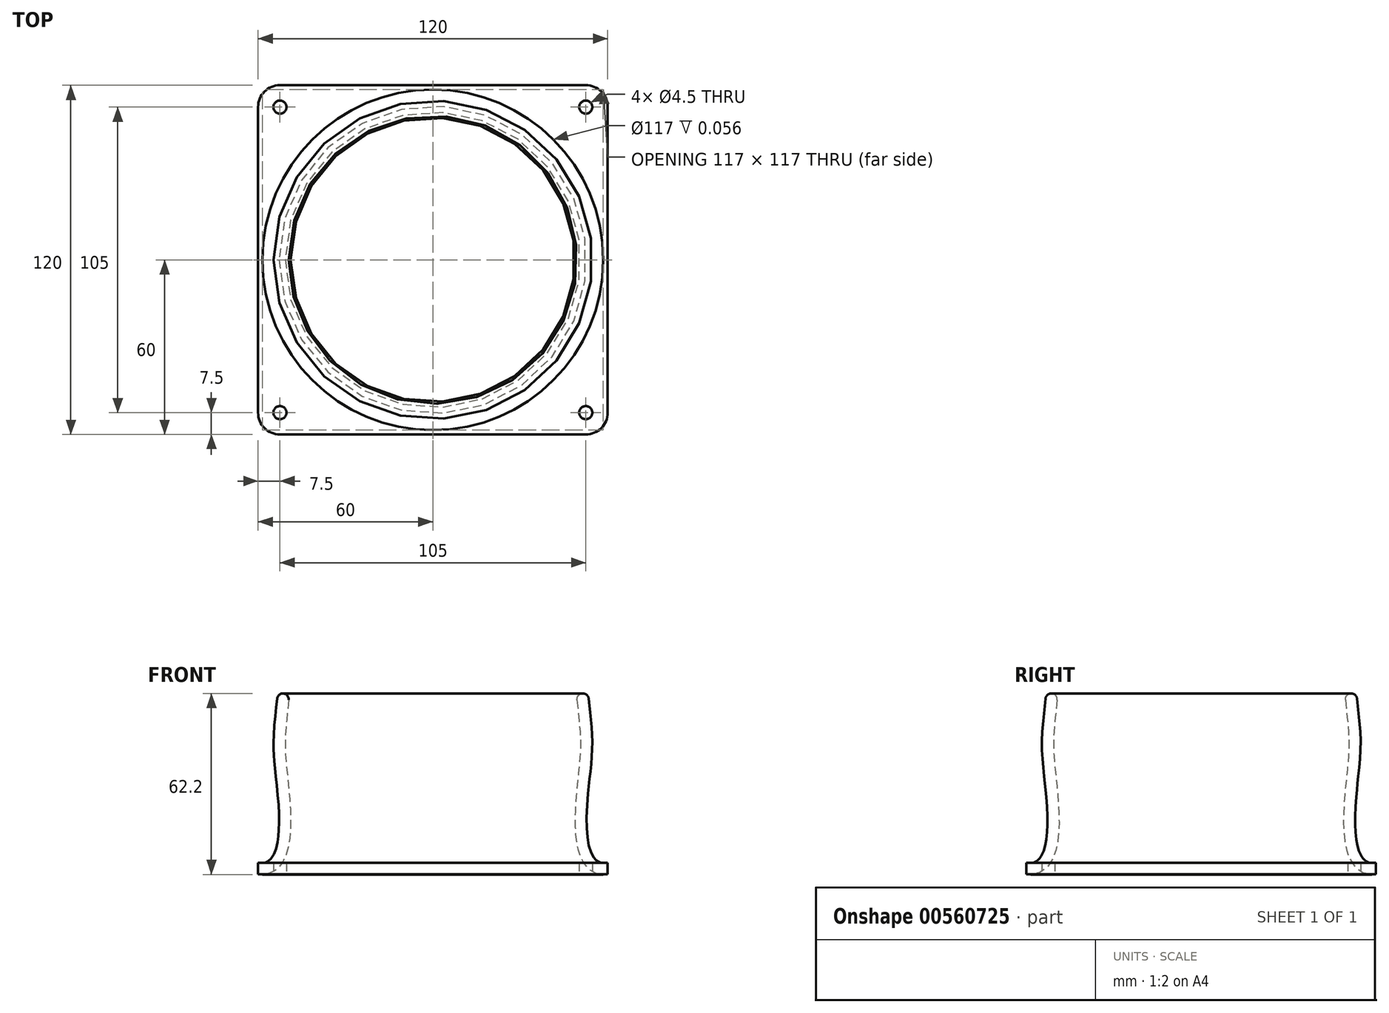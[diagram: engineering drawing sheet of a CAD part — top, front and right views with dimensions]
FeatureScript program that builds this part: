
annotation { "Feature Type Name" : "Feature", "Feature Type Description" : "" }
export const myFeature = defineFeature(function(context is Context, id is Id, definition is map)
    precondition{}
    {
        {
            var Q0;
            Q0=qCreatedBy(makeId("Top.planeOp"),FACE);
            var sketch = newSketch(context, id + "F0", { "sketchPlane" : qUnion([Q0])});
            skLineSegment(sketch, "E0.0", {"start": v(-52.5, 60) * mm, "end": v(52.5, 60) * mm});
            skLineSegment(sketch, "E0.1", {"start": v(-60, -52.5) * mm, "end": v(-60, 52.5) * mm});
            skLineSegment(sketch, "E0.2", {"start": v(-52.5, -60) * mm, "end": v(52.5, -60) * mm});
            skLineSegment(sketch, "E0.3", {"start": v(60, -52.5) * mm, "end": v(60, 52.5) * mm});
            skArc(sketch, "E1", {"start": v(52.5, 60) * mm, "mid": v(57.8, 57.8) * mm, "end": v(60, 52.5) * mm});
            skArc(sketch, "E2.1.1", {"start": v(-60, 52.5) * mm, "mid": v(-57.8, 57.8) * mm, "end": v(-52.5, 60) * mm});
            skArc(sketch, "E2.2.1", {"start": v(-52.5, -60) * mm, "mid": v(-57.8, -57.8) * mm, "end": v(-60, -52.5) * mm});
            skArc(sketch, "E2.3.1", {"start": v(60, -52.5) * mm, "mid": v(57.8, -57.8) * mm, "end": v(52.5, -60) * mm});
            skPoint(sketch, "E2.center", {"position": v(0, 0) * mm});
            skCircle(sketch, "E3", {"center": v(0, 0) * mm, "radius": 58.5 * mm});
            skCircle(sketch, "E4", {"center": v(-52.5, 52.5) * mm, "radius": 2.25 * mm});
            skCircle(sketch, "E5", {"center": v(52.5, 52.5) * mm, "radius": 2.25 * mm});
            skCircle(sketch, "E6", {"center": v(52.5, -52.5) * mm, "radius": 2.25 * mm});
            skCircle(sketch, "E7", {"center": v(-52.5, -52.5) * mm, "radius": 2.25 * mm});
            skSolve(sketch);
        }
        {
            var Q0;
            Q0 = qSketchRegion(id + "F0", true);
            extrude(context, id + "F1", {"entities" : qUnion([Q0]), "depth" : 4 * mm, "offsetDistance" : 25 * mm});
        }
        {
            var Q0;
            Q0=qCreatedBy(makeId("Front.planeOp"),FACE);
            var sketch = newSketch(context, id + "F2", { "sketchPlane" : qUnion([Q0])});
            skPoint(sketch, "E8.0", {"position": v(0, 0) * mm});
            skLineSegment(sketch, "E9", {"start": v(0, 0) * mm, "end": v(0, 73.15) * mm});
            skSolve(sketch);
        }
        {
            var Q0;
            Q0=qCreatedBy(makeId("Front.planeOp"),FACE);
            var sketch = newSketch(context, id + "F3", { "sketchPlane" : qUnion([Q0])});
            skLineSegment(sketch, "E10", {"start": v(-58.5, -0.06) * mm, "end": v(-58.5, 59.94) * mm, "construction": true});
            skLineSegment(sketch, "E11", {"start": v(-58.5, 59.94) * mm, "end": v(-49.5, 59.94) * mm, "construction": true});
            skPoint(sketch, "E12.0", {"position": v(-58.5, -0.06) * mm});
            skFitSpline(sketch, "E13", {"points": [v(-49.5, 59.94) * mm, v(-50.5, 39.94) * mm, v(-49.5, 9.94) * mm, v(-58.5, -0.06) * mm], "startDerivative": vector(-9.13, -94.26) * mm, "endDerivative": vector(-54.03, 0) * mm});
            skFitSpline(sketch, "E14.0", {"points": [v(-53.48, 60.33) * mm, v(-53.86, 56.42) * mm, v(-54.33, 52.1) * mm, v(-54.66, 47.49) * mm, v(-54.72, 44.74) * mm, v(-54.67, 42.44) * mm, v(-54.57, 40.64) * mm, v(-54.42, 38.69) * mm, v(-54.15, 35.9) * mm, v(-53.74, 32.13) * mm, v(-53.25, 27.3) * mm, v(-52.89, 22.4) * mm, v(-52.78, 18.42) * mm, v(-52.86, 15.43) * mm, v(-53.02, 13.32) * mm, v(-53.28, 11.38) * mm, v(-53.76, 9.07) * mm, v(-54.46, 7.18) * mm, v(-55.25, 5.82) * mm, v(-55.87, 5.06) * mm, v(-56.46, 4.54) * mm, v(-57.04, 4.2) * mm, v(-57.67, 4) * mm, v(-58.2, 3.94) * mm, v(-58.5, 3.94) * mm]});
            skArc(sketch, "E15", {"start": v(-49.5, 59.94) * mm, "mid": v(-51.3, 62.13) * mm, "end": v(-53.48, 60.33) * mm});
            skLineSegment(sketch, "E16", {"start": v(-58.5, 3.94) * mm, "end": v(-58.5, 3.94) * mm});
            skLineSegment(sketch, "E17", {"start": v(-58.5, 3.94) * mm, "end": v(-58.5, -0.06) * mm});
            skSolve(sketch);
        }
        {
            var Q0;
            Q0=makeQuery(id+"F3.imprint","IMPRINT",FACE,{"disambiguationData":[TD([[makeQuery(id+"F3.imprint","IMPRINT",EDGE,{"derivedFrom":sQuery(id+"F3.wireOp",EDGE,"E13")}),-1.0]])]});
            var Q1;
            Q1=sQuery(id+"F2.wireOp",EDGE,"E9");
            revolve(context, id + "F4", {"operationType" : NewBodyOperationType.ADD, "entities" : qUnion([Q0]), "axis" : qUnion([Q1]), "revolveType" : RevolveType.FULL});
        }
    });
